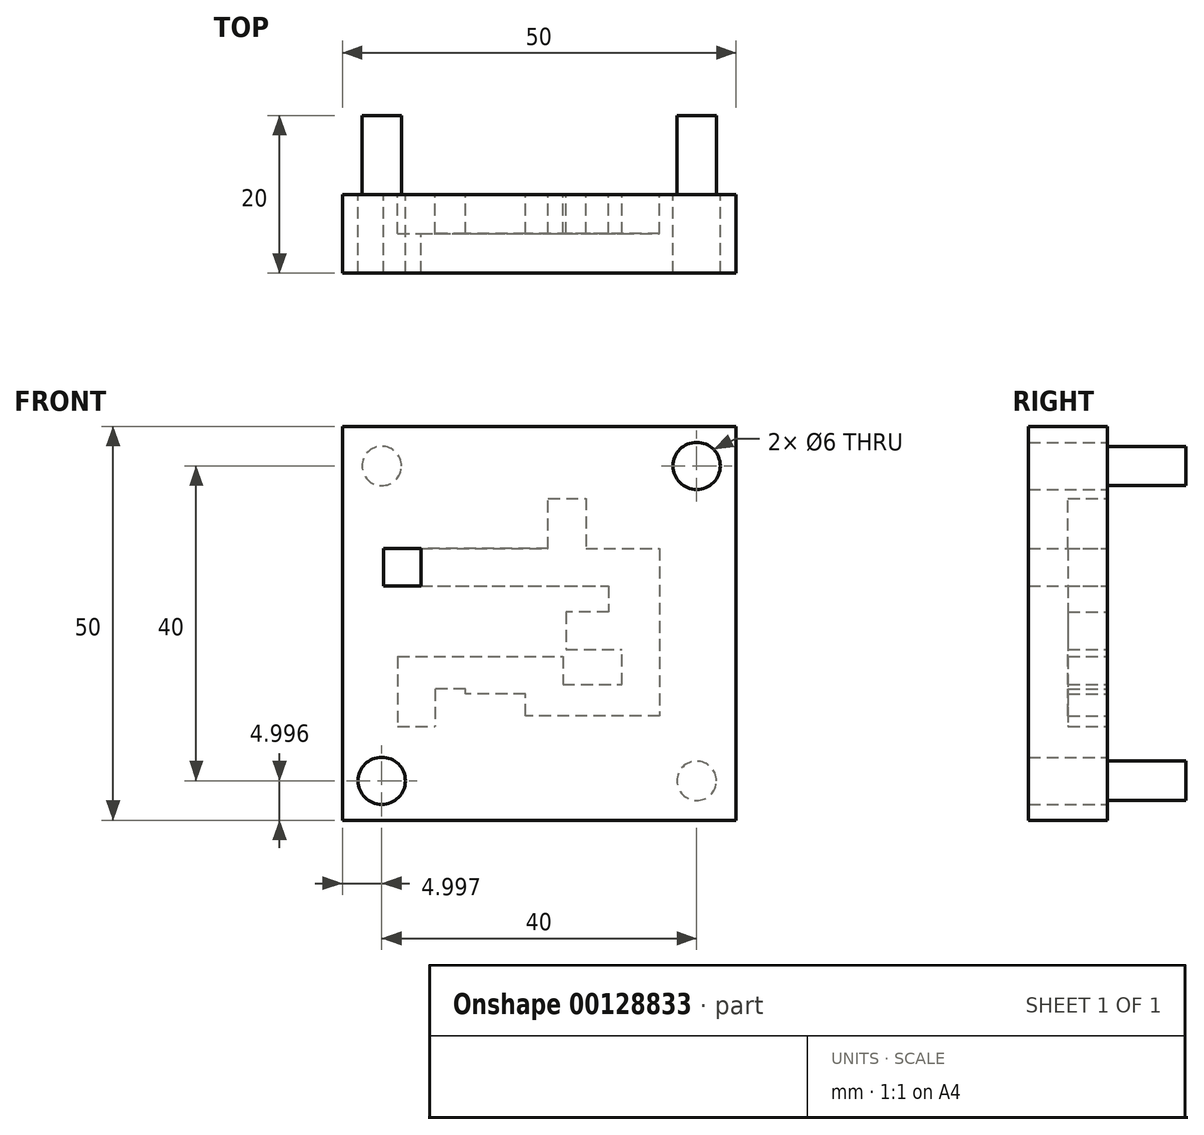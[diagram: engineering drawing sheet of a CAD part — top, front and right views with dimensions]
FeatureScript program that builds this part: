
annotation { "Feature Type Name" : "Feature", "Feature Type Description" : "" }
export const myFeature = defineFeature(function(context is Context, id is Id, definition is map)
    precondition{}
    {
        {
            var Q0;
            Q0=qCreatedBy(makeId("Front.planeOp"),FACE);
            var sketch = newSketch(context, id + "F0", { "sketchPlane" : qUnion([Q0])});
            skLineSegment(sketch, "E0.bottom", {"start": v(7.18, 23.9) * mm, "end": v(-42.82, 23.9) * mm});
            skLineSegment(sketch, "E0.top", {"start": v(7.18, -26.1) * mm, "end": v(-42.82, -26.1) * mm});
            skLineSegment(sketch, "E0.left", {"start": v(7.18, 23.9) * mm, "end": v(7.18, -26.1) * mm});
            skLineSegment(sketch, "E0.right", {"start": v(-42.82, 23.9) * mm, "end": v(-42.82, -26.1) * mm});
            skCircle(sketch, "E1", {"center": v(-37.82, -21.1) * mm, "radius": 3 * mm});
            skCircle(sketch, "E2", {"center": v(2.18, -21.1) * mm, "radius": 2.5 * mm});
            skCircle(sketch, "E3", {"center": v(2.18, 18.9) * mm, "radius": 3 * mm});
            skCircle(sketch, "E4", {"center": v(-37.82, 18.9) * mm, "radius": 2.5 * mm});
            skLineSegment(sketch, "E5.bottom", {"start": v(-32.86, 8.42) * mm, "end": v(-37.62, 8.42) * mm});
            skLineSegment(sketch, "E5.top", {"start": v(-32.86, 3.65) * mm, "end": v(-37.62, 3.65) * mm});
            skLineSegment(sketch, "E5.left", {"start": v(-32.86, 8.42) * mm, "end": v(-32.86, 3.65) * mm});
            skLineSegment(sketch, "E5.right", {"start": v(-37.62, 8.42) * mm, "end": v(-37.62, 3.65) * mm});
            skLineSegment(sketch, "E6", {"start": v(-32.86, 8.42) * mm, "end": v(-16.68, 8.42) * mm});
            skLineSegment(sketch, "E7", {"start": v(-16.68, 8.42) * mm, "end": v(-16.68, 14.8) * mm});
            skLineSegment(sketch, "E8", {"start": v(-16.68, 14.8) * mm, "end": v(-11.91, 14.8) * mm});
            skLineSegment(sketch, "E9", {"start": v(-32.86, 3.65) * mm, "end": v(-16.68, 3.65) * mm});
            skLineSegment(sketch, "E10", {"start": v(-11.91, 14.8) * mm, "end": v(-11.91, 8.42) * mm});
            skLineSegment(sketch, "E11", {"start": v(-11.91, 8.42) * mm, "end": v(-2.53, 8.42) * mm});
            skLineSegment(sketch, "E12", {"start": v(-2.53, 8.42) * mm, "end": v(-2.53, -12.85) * mm});
            skLineSegment(sketch, "E13", {"start": v(-2.53, -12.85) * mm, "end": v(-13.78, -12.85) * mm});
            skLineSegment(sketch, "E14", {"start": v(-16.68, 3.65) * mm, "end": v(-9, 3.65) * mm});
            skLineSegment(sketch, "E15", {"start": v(-13.78, -12.85) * mm, "end": v(-19.58, -12.85) * mm});
            skLineSegment(sketch, "E16", {"start": v(-19.58, -12.85) * mm, "end": v(-19.58, -10.07) * mm});
            skLineSegment(sketch, "E17", {"start": v(-19.58, -10.07) * mm, "end": v(-27.18, -10.07) * mm});
            skLineSegment(sketch, "E18", {"start": v(-9, 3.65) * mm, "end": v(-9, 0.36) * mm});
            skLineSegment(sketch, "E19", {"start": v(-9, 0.36) * mm, "end": v(-14.44, 0.36) * mm});
            skLineSegment(sketch, "E20", {"start": v(-14.44, 0.36) * mm, "end": v(-14.44, -4.4) * mm});
            skLineSegment(sketch, "E21", {"start": v(-14.44, -4.4) * mm, "end": v(-7.3, -4.4) * mm});
            skLineSegment(sketch, "E22", {"start": v(-27.18, -5.3) * mm, "end": v(-14.81, -5.3) * mm});
            skLineSegment(sketch, "E23", {"start": v(-14.81, -5.3) * mm, "end": v(-14.81, -8.87) * mm});
            skLineSegment(sketch, "E24", {"start": v(-14.81, -8.87) * mm, "end": v(-7.3, -8.87) * mm});
            skLineSegment(sketch, "E25", {"start": v(-7.3, -8.87) * mm, "end": v(-7.3, -4.4) * mm});
            skLineSegment(sketch, "E26", {"start": v(-35.8, -14.19) * mm, "end": v(-31.04, -14.19) * mm});
            skLineSegment(sketch, "E27", {"start": v(-35.8, -14.19) * mm, "end": v(-35.8, -9.43) * mm});
            skLineSegment(sketch, "E28", {"start": v(-35.8, -9.43) * mm, "end": v(-31.04, -9.43) * mm});
            skLineSegment(sketch, "E29", {"start": v(-31.04, -9.43) * mm, "end": v(-31.04, -14.19) * mm});
            skLineSegment(sketch, "E30", {"start": v(-27.18, -5.3) * mm, "end": v(-35.8, -5.3) * mm});
            skLineSegment(sketch, "E31", {"start": v(-35.8, -5.3) * mm, "end": v(-35.8, -9.43) * mm});
            skLineSegment(sketch, "E32", {"start": v(-27.18, -10.07) * mm, "end": v(-27.18, -9.43) * mm});
            skLineSegment(sketch, "E33", {"start": v(-27.18, -9.43) * mm, "end": v(-31.04, -9.43) * mm});
            skSolve(sketch);
        }
        {
            var Q0;
            Q0=makeQuery(id+"F0.imprint","IMPRINT",FACE,{"disambiguationData":[TD([[makeQuery(id+"F0.imprint","IMPRINT",EDGE,{"derivedFrom":sQuery(id+"F0.wireOp",EDGE,"E0.bottom")}),1.0]])]});
            extrude(context, id + "F1", {"entities" : qUnion([Q0]), "endBound" : BoundingType.SYMMETRIC, "depth" : 10 * mm});
        }
        {
            var Q0;
            Q0=makeQuery(id+"F0.imprint","IMPRINT",FACE,{"disambiguationData":[TD([[makeQuery(id+"F0.imprint","IMPRINT",EDGE,{"derivedFrom":sQuery(id+"F0.wireOp",EDGE,"E5.left")}),1.0]])]});
            var Q1;
            Q1=makeQuery(id+"F0.imprint","IMPRINT",FACE,{"disambiguationData":[TD([[makeQuery(id+"F0.imprint","IMPRINT",EDGE,{"derivedFrom":sQuery(id+"F0.wireOp",EDGE,"E26")}),1.0]])]});
            extrude(context, id + "F2", {"entities" : qUnion([Q0, Q1]), "operationType" : NewBodyOperationType.ADD, "depth" : 5 * mm});
        }
        {
            var Q0;
            Q0=makeQuery(id+"F0.imprint","IMPRINT",FACE,{"disambiguationData":[TD([[makeQuery(id+"F0.imprint","IMPRINT",EDGE,{"derivedFrom":sQuery(id+"F0.wireOp",EDGE,"E2")}),1.0]])]});
            var Q1;
            Q1=makeQuery(id+"F0.imprint","IMPRINT",FACE,{"disambiguationData":[TD([[makeQuery(id+"F0.imprint","IMPRINT",EDGE,{"derivedFrom":sQuery(id+"F0.wireOp",EDGE,"E4")}),1.0]])]});
            extrude(context, id + "F3", {"entities" : qUnion([Q0, Q1]), "operationType" : NewBodyOperationType.ADD, "oppositeDirection" : true, "depth" : 15 * mm, "hasSecondDirection" : true, "secondDirectionOppositeDirection" : false, "secondDirectionDepth" : 5 * mm});
        }
    });
